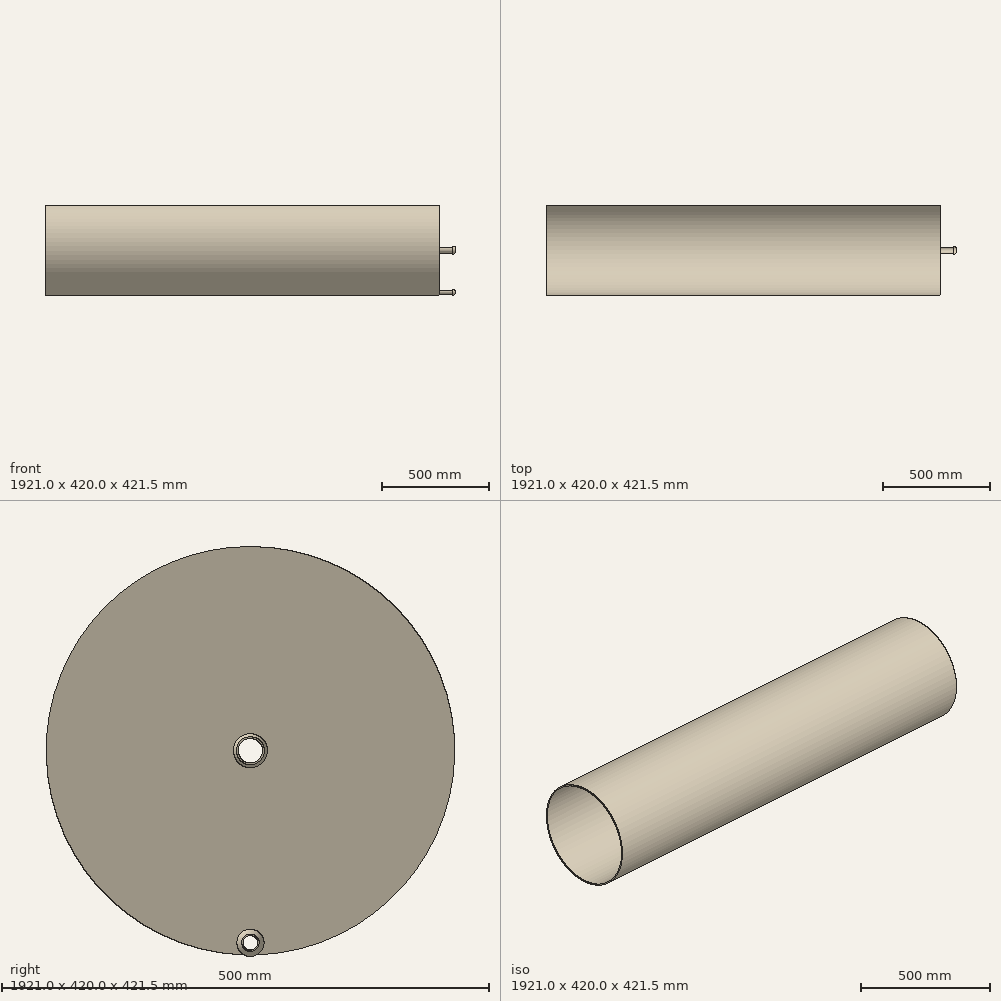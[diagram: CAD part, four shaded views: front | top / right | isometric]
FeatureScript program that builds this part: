
annotation { "Feature Type Name" : "Feature", "Feature Type Description" : "" }
export const myFeature = defineFeature(function(context is Context, id is Id, definition is map)
    precondition{}
    {
        {
            var Q0;
            Q0=qCreatedBy(makeId("Front.planeOp"),FACE);
            var sketch = newSketch(context, id + "F0", { "sketchPlane" : qUnion([Q0])});
            skLineSegment(sketch, "E0.bottom", {"start": v(-1844.8, 210) * mm, "end": v(0, 210) * mm});
            skLineSegment(sketch, "E0.top", {"start": v(-1844.8, 205) * mm, "end": v(0, 205) * mm});
            skLineSegment(sketch, "E0.left", {"start": v(-1844.8, 210) * mm, "end": v(-1844.8, 205) * mm});
            skLineSegment(sketch, "E0.right", {"start": v(0, 210) * mm, "end": v(0, 205) * mm});
            skLineSegment(sketch, "E1", {"start": v(-1844.8, 0) * mm, "end": v(0, 0) * mm, "construction": true});
            skLineSegment(sketch, "E2.bottom", {"start": v(0, 205) * mm, "end": v(-6, 205) * mm});
            skLineSegment(sketch, "E2.top", {"start": v(0, 14.4) * mm, "end": v(-6, 14.4) * mm});
            skLineSegment(sketch, "E2.left", {"start": v(0, 205) * mm, "end": v(0, 14.4) * mm});
            skLineSegment(sketch, "E2.right", {"start": v(-6, 205) * mm, "end": v(-6, 14.4) * mm});
            skLineSegment(sketch, "E3.bottom", {"start": v(-6, 14.4) * mm, "end": v(76.2, 14.4) * mm});
            skLineSegment(sketch, "E3.top", {"start": v(-6, 12.5) * mm, "end": v(76.2, 12.5) * mm});
            skLineSegment(sketch, "E3.left", {"start": v(-6, 14.4) * mm, "end": v(-6, 12.5) * mm});
            skLineSegment(sketch, "E3.right", {"start": v(76.2, 14.4) * mm, "end": v(76.2, 12.5) * mm});
            skCircle(sketch, "E4", {"center": v(66.26, 0) * mm, "radius": 17.5 * mm, "construction": true});
            skLineSegment(sketch, "E5", {"start": v(63.5, 17.28) * mm, "end": v(63.5, 14.4) * mm});
            skArc(sketch, "E6", {"start": v(63.5, 17.28) * mm, "mid": v(70.13, 17.07) * mm, "end": v(76.2, 14.4) * mm});
            skSolve(sketch);
        }
        {
            var Q0;
            Q0 = qSketchRegion(id + "F0", true);
            var Q1;
            Q1=sQuery(id+"F0.wireOp",EDGE,"E1");
            revolve(context, id + "F1", {"entities" : qUnion([Q0]), "axis" : qUnion([Q1]), "revolveType" : RevolveType.FULL});
        }
        {
            var Q0;
            Q0=makeQuery(id+"F1.opRevolve","SWEPT_FACE",FACE,{"disambiguationData":[OSD([sQuery(id+"F0.wireOp",EDGE,"E0.right"),sQuery(id+"F0.wireOp",EDGE,"E2.left")])]});
            var sketch = newSketch(context, id + "F2", { "sketchPlane" : qUnion([Q0])});
            skCircle(sketch, "E7", {"center": v(0, -197.5) * mm, "radius": 7.5 * mm});
            skCircle(sketch, "E8.0", {"center": v(0, 0) * mm, "radius": 205 * mm});
            skSolve(sketch);
        }
        {
            var Q0;
            Q0=makeQuery(id+"F2.imprint","IMPRINT",FACE,{"disambiguationData":[TD([[makeQuery(id+"F2.imprint","IMPRINT",EDGE,{"derivedFrom":sQuery(id+"F2.wireOp",EDGE,"E7")}),1.0]])]});
            var Q1;
            Q1=makeQuery(id+"F2.imprint","IMPRINT",FACE,{"disambiguationData":[TD([[makeQuery(id+"F2.imprint","IMPRINT",EDGE,{"derivedFrom":makeQuery(id+"F1.opRevolve","SWEPT_EDGE",EDGE,{"disambiguationData":[OSD([sQuery(id+"F0.wireOp",EDGE,"E2.left"),sQuery(id+"F0.wireOp",EDGE,"E3.bottom")])]})}),-1.0]])]});
            extrude(context, id + "F3", {"entities" : qUnion([Q0, Q1]), "operationType" : NewBodyOperationType.REMOVE, "oppositeDirection" : true, "depth" : 25.4 * mm, "offsetDistance" : 25.4 * mm});
        }
        {
            var Q0;
            Q0=makeQuery(id+"F1.opRevolve","SWEPT_FACE",FACE,{"disambiguationData":[OSD([sQuery(id+"F0.wireOp",EDGE,"E0.right"),sQuery(id+"F0.wireOp",EDGE,"E2.left")])]});
            var sketch = newSketch(context, id + "F4", { "sketchPlane" : qUnion([Q0])});
            skCircle(sketch, "E9.0", {"center": v(0, -197.5) * mm, "radius": 7.5 * mm});
            skCircle(sketch, "E10", {"center": v(0, -197.5) * mm, "radius": 9 * mm});
            skSolve(sketch);
        }
        {
            var Q0;
            Q0 = qSketchRegion(id + "F4", true);
            extrude(context, id + "F5", {"entities" : qUnion([Q0]), "operationType" : NewBodyOperationType.ADD, "depth" : 76.2 * mm, "offsetDistance" : 25.4 * mm});
        }
        {
            var Q0;
            Q0=qCreatedBy(makeId("Front.planeOp"),FACE);
            var sketch = newSketch(context, id + "F6", { "sketchPlane" : qUnion([Q0])});
            skLineSegment(sketch, "E11", {"start": v(0, -188.5) * mm, "end": v(76.2, -188.5) * mm});
            skLineSegment(sketch, "E12", {"start": v(76.2, -206.5) * mm, "end": v(0, -206.5) * mm});
            skCircle(sketch, "E13", {"center": v(65.48, -197.5) * mm, "radius": 14 * mm, "construction": true});
            skLineSegment(sketch, "E14", {"start": v(0, -188.5) * mm, "end": v(0, -206.5) * mm, "construction": true});
            skLineSegment(sketch, "E15", {"start": v(76.2, -206.5) * mm, "end": v(76.2, -188.5) * mm, "construction": true});
            skLineSegment(sketch, "E16", {"start": v(76.2, -197.5) * mm, "end": v(0, -197.5) * mm, "construction": true});
            skLineSegment(sketch, "E17", {"start": v(62.23, -183.88) * mm, "end": v(62.23, -188.5) * mm});
            skLineSegment(sketch, "E18", {"start": v(62.23, -188.5) * mm, "end": v(76.2, -188.5) * mm});
            skArc(sketch, "E19", {"start": v(76.2, -188.5) * mm, "mid": v(69.87, -184.2) * mm, "end": v(62.23, -183.88) * mm});
            skSolve(sketch);
        }
        {
            var Q0;
            Q0 = qSketchRegion(id + "F6", true);
            var Q1;
            Q1=sQuery(id+"F6.wireOp",EDGE,"E16");
            revolve(context, id + "F7", {"operationType" : NewBodyOperationType.ADD, "entities" : qUnion([Q0]), "axis" : qUnion([Q1]), "revolveType" : RevolveType.FULL});
        }
    });
